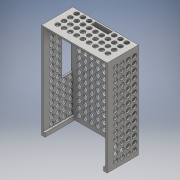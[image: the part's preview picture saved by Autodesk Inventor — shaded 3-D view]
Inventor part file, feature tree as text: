
AUTODESK INVENTOR PART (.ipt)
format: ipt  version: 2016 (Build 200138000, 138)  size: 583,680 bytes
history: native  units: mm
features: sketch x12, extrude x8, hole x2
ambient origin geometry x8: Origin, YZ Plane, XZ Plane, XY Plane, X Axis, Y Axis, Z Axis, Center Point
bodies: Solid1 (feature_tree)
feature tree (22):
  extrude  "Extrusion1"  Depth=60.0mm
  extrude  "Extrusion3"  Depth=6.0mm
  extrude  "Extrusion5"  Depth=6.0mm
  extrude  "Extrusion7"  Depth=90.0mm
  hole  "Hole1"  [1 undecoded]
  hole  "Hole2"  [1 undecoded]
  extrude  "Extrusion8"  Depth=4.3mm
  extrude  "Extrusion9"  Depth=6.0mm
  extrude  "Extrusion10"  Depth=27.0mm
  sketch  "Sketch14"  dims[d19=45.0mm d20=1.5mm d21=0.0mm]
  extrude  "Extrusion11"  Depth=1.5mm TaperAngle=0.0deg
  sketch  "Sketch16"  dims[d26=30.0mm d27=1.5mm d28=0.0mm d31=90.0mm d32=30.0mm d33=1.5mm d34=0.0mm d40=63.0mm d41=1.5mm d42=30.0mm d43=0.0mm d44=4.3mm d46=7.5mm d47=4.3mm d48=6.0mm d49=3.0mm d50=3.0mm d51=3.0mm d52=3.0mm d53=3.0mm d54=4.3mm d55=6.0mm d56=4.0mm d57=2.0mm d58=90.0deg d59=8.0mm d60=0.0mm d61=4.3mm d62=3.8mm d63=7.5mm d64=4.3mm d65=6.0mm d66=4.3mm d67=6.0mm d68=4.3mm d69=3.0mm d70=3.0mm d71=3.0mm d72=3.0mm d73=4.3mm d74=6.0mm d75=4.0mm d76=2.0mm d77=90.0deg d78=8.0mm d79=0.0mm d80=30.0mm d81=0.0mm d82=3.7mm d83=2.0mm d84=0.0mm d85=3.7mm d86=2.0mm d87=0.0mm d89=2.0mm d90=0.0mm d93=11.0mm d95=5.5mm]
  sketch  "Sketch1"  dims[d0=60.0mm d1=4.3mm]
  sketch  "Sketch3"  dims[d2=6.0mm d3=6.0mm]
  sketch  "Sketch5"  dims[d4=4.3mm d5=6.0mm]
  sketch  "Sketch8"  dims[d6=90.0mm d7=4.3mm]
  sketch  "Sketch9"  dims[d8=6.0mm d9=4.3mm]
  sketch  "Sketch10"  dims[d10=15.0mm d12=27.0mm]
  sketch  "Sketch11"  dims[d13=4.3mm d14=4.3mm]
  sketch  "Sketch12"  dims[d15=6.0mm d16=6.0mm]
  sketch  "Sketch13"  dims[d17=15.0mm d18=27.0mm]
  sketch  "Sketch15"  dims[d25=90.0mm]
note: 2 required parameter values undecoded (feature->parameter linkage not recoverable at this tier; creation-order binding heuristic only, values carry confidence <= 0.55)
